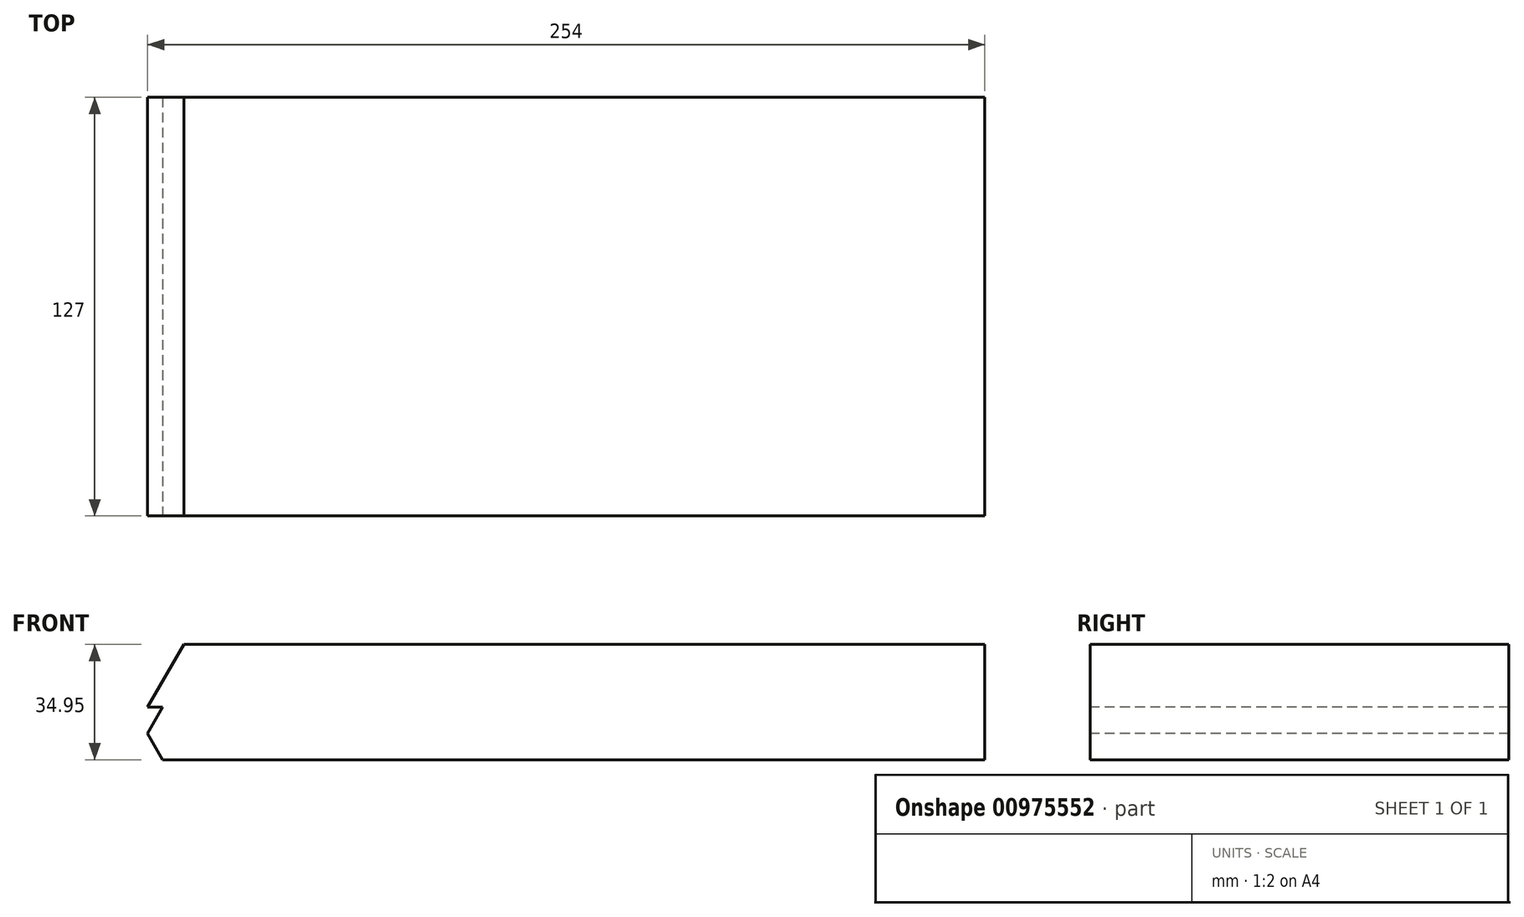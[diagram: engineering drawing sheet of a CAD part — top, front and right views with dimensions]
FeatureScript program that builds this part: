
annotation { "Feature Type Name" : "Feature", "Feature Type Description" : "" }
export const myFeature = defineFeature(function(context is Context, id is Id, definition is map)
    precondition{}
    {
        {
            var Q0;
            Q0=qCreatedBy(makeId("Top.planeOp"),FACE);
            var sketch = newSketch(context, id + "F0", { "sketchPlane" : qUnion([Q0])});
            skLineSegment(sketch, "E0.bottom", {"start": v(-116.56, 42.51) * mm, "end": v(137.44, 42.51) * mm});
            skLineSegment(sketch, "E0.top", {"start": v(-116.56, -84.49) * mm, "end": v(137.44, -84.49) * mm});
            skLineSegment(sketch, "E0.left", {"start": v(-116.56, 42.51) * mm, "end": v(-116.56, -84.49) * mm});
            skLineSegment(sketch, "E0.right", {"start": v(137.44, 42.51) * mm, "end": v(137.44, -84.49) * mm});
            skPoint(sketch, "E1", {"position": v(-116.56, 42.51) * mm});
            skPoint(sketch, "E2", {"position": v(137.44, -84.49) * mm});
            skSolve(sketch);
        }
        {
            var Q0;
            Q0=qSketchRegion(id+"F0",true);
            extrude(context, id + "F1", {"entities" : qUnion([Q0]), "oppositeDirection" : true, "depth" : 15.9 * mm, "offsetDistance" : 25.4 * mm});
        }
        {
            var Q0;
            Q0=makeQuery(id+"F1.opExtrude","SWEPT_FACE",FACE,{"disambiguationData":[OSD([sQuery(id+"F0.wireOp",EDGE,"E0.top")])]});
            var sketch = newSketch(context, id + "F2", { "sketchPlane" : qUnion([Q0])});
            skPoint(sketch, "E3", {"position": v(-116.56, -7.95) * mm});
            skLineSegment(sketch, "E4", {"start": v(-116.56, -7.95) * mm, "end": v(-111.97, 0) * mm});
            skLineSegment(sketch, "E5", {"start": v(-111.97, 0) * mm, "end": v(-116.56, 0) * mm});
            skLineSegment(sketch, "E6", {"start": v(-116.56, 0) * mm, "end": v(-116.56, -7.95) * mm});
            skLineSegment(sketch, "E7", {"start": v(-116.56, -15.9) * mm, "end": v(-111.97, -15.9) * mm});
            skLineSegment(sketch, "E8", {"start": v(-111.97, -15.9) * mm, "end": v(-116.56, -7.95) * mm});
            skSolve(sketch);
        }
        {
            var Q0;
            Q0=makeQuery(id+"F2.imprint","IMPRINT",FACE,{"disambiguationData":[TD([[makeQuery(id+"F2.imprint","IMPRINT",EDGE,{"derivedFrom":sQuery(id+"F2.wireOp",EDGE,"E4")}),1.0]])]});
            var Q1;
            {var subQ0=sQuery(id+"F2.wireOp",EDGE,"E7");Q1=makeQuery(id+"F2.imprint","IMPRINT",FACE,{"disambiguationData":[TD([[makeQuery(id+"F2.imprint","IMPRINT",EDGE,{"derivedFrom":subQ0}),1.0]])]});}
            extrude(context, id + "F3", {"entities" : qUnion([Q0, Q1]), "operationType" : NewBodyOperationType.REMOVE, "oppositeDirection" : true, "depth" : 127 * mm, "offsetDistance" : 25.4 * mm});
        }
        {
            var Q0;
            Q0=makeQuery(id+"F1.opExtrude","CAP_FACE",FACE,{"disambiguationData":[OSD([sQuery(id+"F0.wireOp",EDGE,"E0.bottom"),sQuery(id+"F0.wireOp",EDGE,"E0.top"),sQuery(id+"F0.wireOp",EDGE,"E0.left"),sQuery(id+"F0.wireOp",EDGE,"E0.right")])],"isStart":true});
            var sketch = newSketch(context, id + "F4", { "sketchPlane" : qUnion([Q0])});
            skLineSegment(sketch, "E9.bottom", {"start": v(-116.56, 42.51) * mm, "end": v(137.44, 42.51) * mm});
            skLineSegment(sketch, "E9.top", {"start": v(-116.56, -84.49) * mm, "end": v(137.44, -84.49) * mm});
            skLineSegment(sketch, "E9.left", {"start": v(-116.56, 42.51) * mm, "end": v(-116.56, -84.49) * mm});
            skLineSegment(sketch, "E9.right", {"start": v(137.44, 42.51) * mm, "end": v(137.44, -84.49) * mm});
            skSolve(sketch);
        }
        {
            var Q0;
            {var subQ1=sQuery(id+"F4.wireOp",EDGE,"E9.bottom");Q0=makeQuery(id+"F4.imprint","IMPRINT",FACE,{"disambiguationData":[TD([[makeQuery(id+"F4.imprint","IMPRINT",EDGE,{"derivedFrom":subQ1}),-1.0]])]});}
            extrude(context, id + "F5", {"entities" : qUnion([Q0]), "operationType" : NewBodyOperationType.ADD, "depth" : 19.05 * mm, "offsetDistance" : 25.4 * mm});
        }
        {
            var Q0;
            Q0=makeQuery(id+"F5.boolean.opBoolean","MERGE",FACE,{"derivedFrom":[makeQuery(id+"F1.opExtrude","SWEPT_FACE",FACE,{"disambiguationData":[OSD([sQuery(id+"F0.wireOp",EDGE,"E0.top")])]}),makeQuery(id+"F5.opExtrude","SWEPT_FACE",FACE,{"disambiguationData":[OSD([sQuery(id+"F4.wireOp",EDGE,"E9.top")])]})]});
            var sketch = newSketch(context, id + "F6", { "sketchPlane" : qUnion([Q0])});
            skLineSegment(sketch, "E10", {"start": v(-116.56, 0) * mm, "end": v(-105.56, 19.05) * mm});
            skLineSegment(sketch, "E11", {"start": v(-105.56, 19.05) * mm, "end": v(-116.56, 19.05) * mm});
            skLineSegment(sketch, "E12", {"start": v(-116.56, 19.05) * mm, "end": v(-116.56, 0) * mm});
            skSolve(sketch);
        }
        {
            var Q0;
            Q0 = qSketchRegion(id + "F6", true);
            extrude(context, id + "F7", {"entities" : qUnion([Q0]), "operationType" : NewBodyOperationType.REMOVE, "oppositeDirection" : true, "depth" : 127 * mm, "offsetDistance" : 25.4 * mm});
        }
        {
            var Q0;
            Q0=makeQuery(id+"F5.boolean.opBoolean","MERGE",FACE,{"derivedFrom":[makeQuery(id+"F1.opExtrude","SWEPT_FACE",FACE,{"disambiguationData":[OSD([sQuery(id+"F0.wireOp",EDGE,"E0.top")])]}),makeQuery(id+"F5.opExtrude","SWEPT_FACE",FACE,{"disambiguationData":[OSD([sQuery(id+"F4.wireOp",EDGE,"E9.top")])]})]});
            var sketch = newSketch(context, id + "F8", { "sketchPlane" : qUnion([Q0])});
            skLineSegment(sketch, "E13", {"start": v(-111.97, 0) * mm, "end": v(137.44, 0) * mm});
            skSolve(sketch);
        }
        {
            var Q0;
            Q0=sQuery(id+"F8.wireOp",EDGE,"E13");
            extrude(context, id + "F9", {"bodyType" : ToolBodyType.SURFACE, "surfaceEntities" : qUnion([Q0]), "oppositeDirection" : true, "depth" : 127 * mm, "offsetDistance" : 25.4 * mm});
        }
    });
